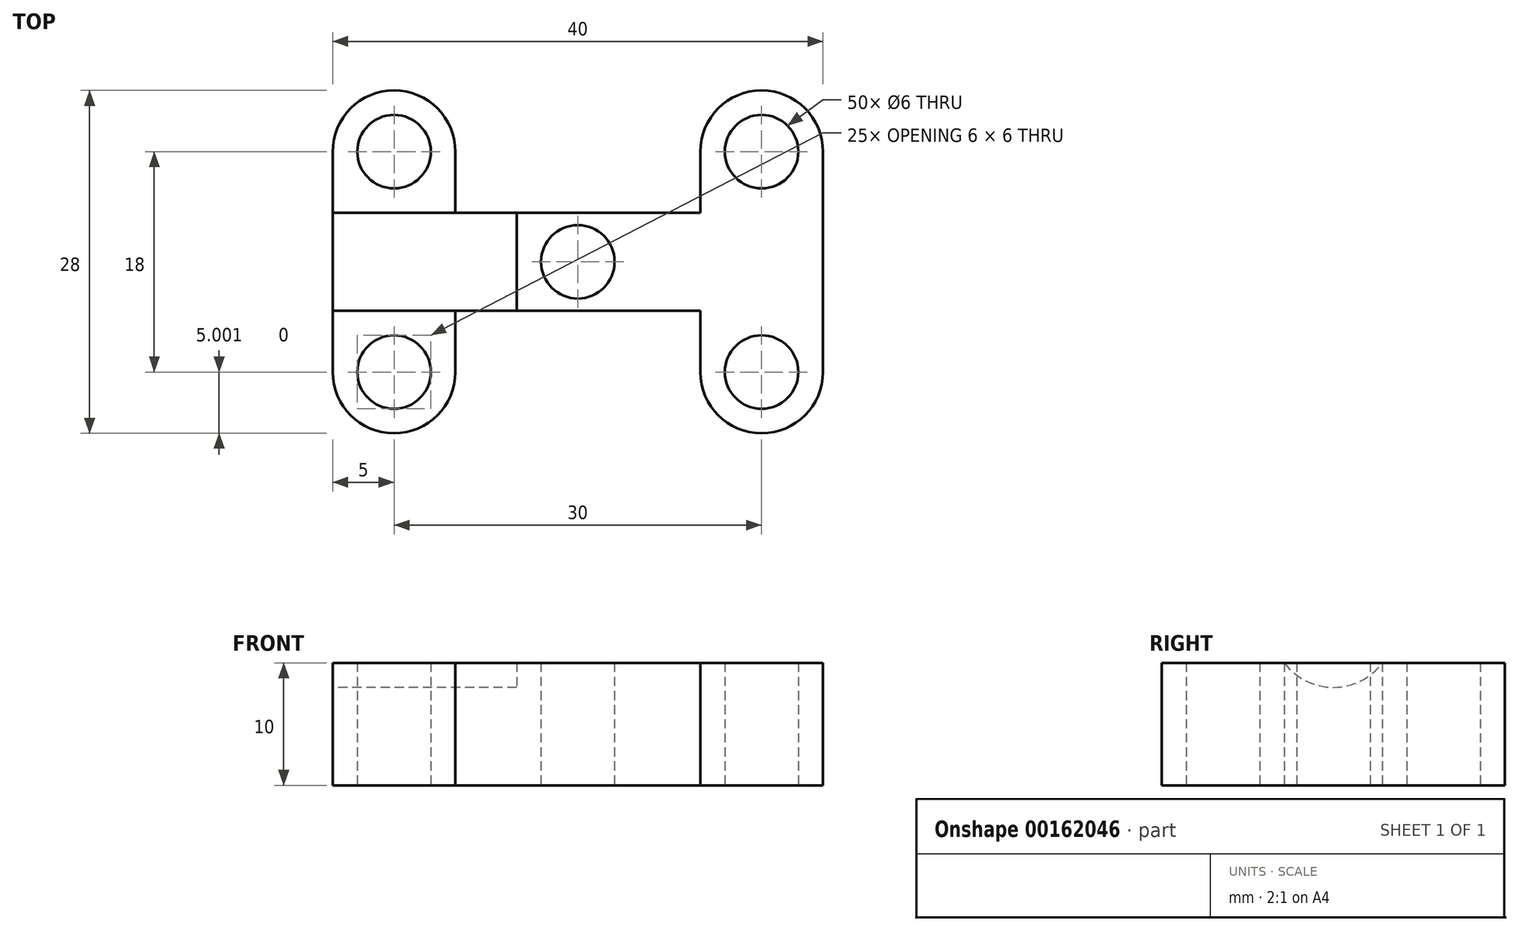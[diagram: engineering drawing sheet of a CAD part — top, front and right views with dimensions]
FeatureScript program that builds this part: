
annotation { "Feature Type Name" : "Feature", "Feature Type Description" : "" }
export const myFeature = defineFeature(function(context is Context, id is Id, definition is map)
    precondition{}
    {
        {
            var Q0;
            Q0=qCreatedBy(makeId("Front.planeOp"),FACE);
            var sketch = newSketch(context, id + "F0", { "sketchPlane" : qUnion([Q0])});
            skLineSegment(sketch, "E0.bottom", {"start": v(-25, 5) * mm, "end": v(25, 5) * mm});
            skLineSegment(sketch, "E0.top", {"start": v(-25, -5) * mm, "end": v(25, -5) * mm});
            skLineSegment(sketch, "E0.left", {"start": v(-25, 5) * mm, "end": v(-25, -5) * mm});
            skLineSegment(sketch, "E0.right", {"start": v(25, 5) * mm, "end": v(25, -5) * mm});
            skPoint(sketch, "E0.middle", {"position": v(0, 0) * mm});
            skLineSegment(sketch, "E1.bottom", {"start": v(-25, 5) * mm, "end": v(-10, 5) * mm});
            skLineSegment(sketch, "E1.top", {"start": v(-25, 90) * mm, "end": v(-10, 90) * mm});
            skLineSegment(sketch, "E1.left", {"start": v(-25, 5) * mm, "end": v(-25, 90) * mm});
            skLineSegment(sketch, "E1.right", {"start": v(-10, 5) * mm, "end": v(-10, 90) * mm});
            skLineSegment(sketch, "E2.MirrorCS", {"start": v(10, 5) * mm, "end": v(10, 90) * mm});
            skLineSegment(sketch, "E3.MirrorCS", {"start": v(25, 5) * mm, "end": v(25, 90) * mm});
            skLineSegment(sketch, "E4.MirrorCS", {"start": v(25, 5) * mm, "end": v(10, 5) * mm});
            skLineSegment(sketch, "E5.MirrorCS", {"start": v(25, 90) * mm, "end": v(10, 90) * mm});
            skPoint(sketch, "E6", {"position": v(-17.5, 80) * mm});
            skPoint(sketch, "E6.positionSnap0", {"position": v(-17.5, 90) * mm});
            skPoint(sketch, "E7.MirrorP", {"position": v(17.5, 80) * mm});
            skLineSegment(sketch, "E8", {"start": v(10, 5) * mm, "end": v(10, -5) * mm});
            skLineSegment(sketch, "E9", {"start": v(-10, 5) * mm, "end": v(-10, -5) * mm});
            skLineSegment(sketch, "E10.bottom", {"start": v(-25, 90) * mm, "end": v(25, 90) * mm});
            skLineSegment(sketch, "E10.top", {"start": v(-25, 95) * mm, "end": v(25, 95) * mm});
            skLineSegment(sketch, "E10.left", {"start": v(-25, 90) * mm, "end": v(-25, 95) * mm});
            skLineSegment(sketch, "E10.right", {"start": v(25, 90) * mm, "end": v(25, 95) * mm});
            skLineSegment(sketch, "E11", {"start": v(-10, 90) * mm, "end": v(-10, 95) * mm});
            skLineSegment(sketch, "E12", {"start": v(10, 90) * mm, "end": v(10, 95) * mm});
            skPoint(sketch, "E12.endSnap0", {"position": v(0, 95) * mm});
            skSolve(sketch);
        }
        {
            var Q0;
            Q0=qCreatedBy(makeId("Top.planeOp"),FACE);
            var sketch = newSketch(context, id + "F1", { "sketchPlane" : qUnion([Q0])});
            skLineSegment(sketch, "E13", {"start": v(-25, -6.7) * mm, "end": v(25, -6.7) * mm});
            skLineSegment(sketch, "E14", {"start": v(-25, -14.7) * mm, "end": v(15, -14.7) * mm});
            skLineSegment(sketch, "E15.bottom", {"start": v(-25, 3.3) * mm, "end": v(15, 3.3) * mm});
            skLineSegment(sketch, "E15.top", {"start": v(-25, -24.7) * mm, "end": v(15, -24.7) * mm});
            skLineSegment(sketch, "E15.left", {"start": v(-25, 3.3) * mm, "end": v(-25, -24.7) * mm});
            skLineSegment(sketch, "E15.right", {"start": v(15, 3.3) * mm, "end": v(15, -24.7) * mm});
            skLineSegment(sketch, "E16", {"start": v(-15, 3.3) * mm, "end": v(-15, -24.7) * mm});
            skLineSegment(sketch, "E17", {"start": v(5, 3.3) * mm, "end": v(5, -24.7) * mm});
            skPoint(sketch, "E18", {"position": v(10, -19.7) * mm});
            skLineSegment(sketch, "E19", {"start": v(-25, -10.7) * mm, "end": v(15, -10.7) * mm, "construction": true});
            skPoint(sketch, "E20.MirrorP", {"position": v(10, -1.7) * mm});
            skPoint(sketch, "E21", {"position": v(-5, -10.7) * mm});
            skLineSegment(sketch, "E22", {"start": v(-5, 3.3) * mm, "end": v(-5, -24.7) * mm, "construction": true});
            skPoint(sketch, "E23.MirrorP", {"position": v(-20, -1.7) * mm});
            skPoint(sketch, "E24.MirrorP", {"position": v(-20, -19.7) * mm});
            skSolve(sketch);
        }
        {
            var Q0;
            {var subQ0=sQuery(id+"F1.wireOp",EDGE,"E15.left");var subQ1=sQuery(id+"F1.wireOp",EDGE,"E13");var subQ2=makeQuery(id+"F1.imprint","INTERSECT",VERTEX,{"derivedFrom":[subQ1,subQ0]});Q0=makeQuery(id+"F1.imprint","IMPRINT",FACE,{"disambiguationData":[TD([[makeQuery(id+"F1.imprint","IMPRINT",EDGE,{"disambiguationData":[TD([[subQ2,-1.0]])],"derivedFrom":subQ1}),1.0]])]});}
            var Q1;
            {var subQ0=sQuery(id+"F1.wireOp",EDGE,"E15.left");var subQ1=sQuery(id+"F1.wireOp",EDGE,"E14");var subQ2=makeQuery(id+"F1.imprint","INTERSECT",VERTEX,{"derivedFrom":[subQ1,subQ0]});Q1=makeQuery(id+"F1.imprint","IMPRINT",FACE,{"disambiguationData":[TD([[makeQuery(id+"F1.imprint","IMPRINT",EDGE,{"disambiguationData":[TD([[subQ2,-1.0]])],"derivedFrom":subQ1}),-1.0]])]});}
            var Q2;
            {var subQ0=sQuery(id+"F1.wireOp",EDGE,"E15.right");var subQ1=sQuery(id+"F1.wireOp",EDGE,"E13");var subQ2=makeQuery(id+"F1.imprint","INTERSECT",VERTEX,{"derivedFrom":[subQ1,subQ0]});Q2=makeQuery(id+"F1.imprint","IMPRINT",FACE,{"disambiguationData":[TD([[makeQuery(id+"F1.imprint","IMPRINT",EDGE,{"disambiguationData":[TD([[subQ2,1.0]])],"derivedFrom":subQ1}),1.0]])]});}
            var Q3;
            {var subQ0=sQuery(id+"F1.wireOp",EDGE,"E15.right");var subQ1=sQuery(id+"F1.wireOp",EDGE,"E14");var subQ2=makeQuery(id+"F1.imprint","INTERSECT",VERTEX,{"derivedFrom":[subQ1,subQ0]});Q3=makeQuery(id+"F1.imprint","IMPRINT",FACE,{"disambiguationData":[TD([[makeQuery(id+"F1.imprint","IMPRINT",EDGE,{"disambiguationData":[TD([[subQ2,1.0]])],"derivedFrom":subQ1}),-1.0]])]});}
            extrude(context, id + "F2", {"entities" : qUnion([Q0, Q1, Q2, Q3]), "depth" : 10 * mm});
        }
        {
            var Q0;
            {var subQ0=sQuery(id+"F1.wireOp",EDGE,"E15.left");var subQ1=sQuery(id+"F1.wireOp",EDGE,"E13");var subQ2=makeQuery(id+"F1.imprint","INTERSECT",VERTEX,{"derivedFrom":[subQ1,subQ0]});Q0=makeQuery(id+"F1.imprint","IMPRINT",FACE,{"disambiguationData":[TD([[makeQuery(id+"F1.imprint","IMPRINT",EDGE,{"disambiguationData":[TD([[subQ2,-1.0]])],"derivedFrom":subQ1}),-1.0]])]});}
            var Q1;
            {var subQ0=sQuery(id+"F1.wireOp",EDGE,"E16");var subQ1=sQuery(id+"F1.wireOp",EDGE,"E13");var subQ2=makeQuery(id+"F1.imprint","INTERSECT",VERTEX,{"derivedFrom":[subQ1,subQ0]});Q1=makeQuery(id+"F1.imprint","IMPRINT",FACE,{"disambiguationData":[TD([[makeQuery(id+"F1.imprint","IMPRINT",EDGE,{"disambiguationData":[TD([[subQ2,-1.0]])],"derivedFrom":subQ1}),-1.0]])]});}
            var Q2;
            {var subQ0=sQuery(id+"F1.wireOp",EDGE,"E15.right");var subQ1=sQuery(id+"F1.wireOp",EDGE,"E13");var subQ2=makeQuery(id+"F1.imprint","INTERSECT",VERTEX,{"derivedFrom":[subQ1,subQ0]});Q2=makeQuery(id+"F1.imprint","IMPRINT",FACE,{"disambiguationData":[TD([[makeQuery(id+"F1.imprint","IMPRINT",EDGE,{"disambiguationData":[TD([[subQ2,1.0]])],"derivedFrom":subQ1}),-1.0]])]});}
            extrude(context, id + "F3", {"entities" : qUnion([Q0, Q1, Q2]), "depth" : 10 * mm});
        }
        {
            var Q0;
            Q0=makeQuery(id+"F3.opExtrude","SWEPT_FACE",FACE,{"disambiguationData":[OSD([sQuery(id+"F1.wireOp",EDGE,"E15.left")])]});
            var sketch = newSketch(context, id + "F4", { "sketchPlane" : qUnion([Q0])});
            skArc(sketch, "E25", {"start": v(6.7, 10) * mm, "mid": v(10.7, 8) * mm, "end": v(14.7, 10) * mm});
            skSolve(sketch);
        }
        {
            var Q0;
            Q0=makeQuery(id+"F4.imprint","IMPRINT",FACE,{"disambiguationData":[TD([[makeQuery(id+"F4.imprint","IMPRINT",EDGE,{"derivedFrom":sQuery(id+"F4.wireOp",EDGE,"E25")}),1.0]])]});
            extrude(context, id + "F5", {"entities" : qUnion([Q0]), "operationType" : NewBodyOperationType.REMOVE, "oppositeDirection" : true, "depth" : 15 * mm});
        }
        {
            var Q0;
            Q0=sQuery(id+"F1.wireOp",VERTEX,"E23.MirrorP");
            var Q1;
            Q1=sQuery(id+"F1.wireOp",VERTEX,"E21");
            var Q2;
            Q2=sQuery(id+"F1.wireOp",VERTEX,"E20.MirrorP");
            var Q3;
            Q3=sQuery(id+"F1.wireOp",VERTEX,"E18");
            var Q4;
            Q4=sQuery(id+"F1.wireOp",VERTEX,"E24.MirrorP");
            var Q5;
            Q5=makeQuery(id+"F2.opExtrude","SWEPT_BODY",BODY,{"disambiguationData":[OSD([sQuery(id+"F1.wireOp",EDGE,"E13"),sQuery(id+"F1.wireOp",EDGE,"E15.bottom"),sQuery(id+"F1.wireOp",EDGE,"E15.left"),sQuery(id+"F1.wireOp",EDGE,"E15.right")])]});
            var Q6;
            Q6=makeQuery(id+"F3.opExtrude","SWEPT_BODY",BODY,{"disambiguationData":[OSD([sQuery(id+"F1.wireOp",EDGE,"E13"),sQuery(id+"F1.wireOp",EDGE,"E14"),sQuery(id+"F1.wireOp",EDGE,"E15.left"),sQuery(id+"F1.wireOp",EDGE,"E15.right")])]});
            var Q7;
            Q7=makeQuery(id+"F2.opExtrude","SWEPT_BODY",BODY,{"disambiguationData":[OSD([sQuery(id+"F1.wireOp",EDGE,"E14"),sQuery(id+"F1.wireOp",EDGE,"E15.top"),sQuery(id+"F1.wireOp",EDGE,"E15.left"),sQuery(id+"F1.wireOp",EDGE,"E15.right")])]});
            hole(context, id + "F6", {"style" : HoleStyle.SIMPLE, "endStyle" : HoleEndStyle.BLIND, "oppositeDirection" : true, "holeDiameter" : 6 * mm, "holeDepth" : 20 * mm, "locations" : qUnion([Q0, Q1, Q2, Q3, Q4]), "scope" : qUnion([Q5, Q6, Q7])});
        }
        {
            var Q0;
            Q0=makeQuery(id+"F2.opExtrude","SWEPT_EDGE",EDGE,{"disambiguationData":[OSD([sQuery(id+"F1.wireOp",EDGE,"E15.bottom"),sQuery(id+"F1.wireOp",EDGE,"E15.left")])]});
            var Q1;
            Q1=makeQuery(id+"F2.opExtrude","SWEPT_EDGE",EDGE,{"disambiguationData":[OSD([sQuery(id+"F1.wireOp",EDGE,"E15.top"),sQuery(id+"F1.wireOp",EDGE,"E15.left")])]});
            var Q2;
            Q2=makeQuery(id+"F2.opExtrude","SWEPT_EDGE",EDGE,{"disambiguationData":[OSD([sQuery(id+"F1.wireOp",EDGE,"E15.top"),sQuery(id+"F1.wireOp",EDGE,"E15.right")])]});
            var Q3;
            Q3=makeQuery(id+"F2.opExtrude","SWEPT_EDGE",EDGE,{"disambiguationData":[OSD([sQuery(id+"F1.wireOp",EDGE,"E15.bottom"),sQuery(id+"F1.wireOp",EDGE,"E15.right")])]});
            fillet(context, id + "F7", {"entities" : qUnion([Q0, Q1, Q2, Q3]), "radius" : 5 * mm, "tangentPropagation" : true, "allowEdgeOverflow" : false});
        }
        {
            var Q0;
            Q0=makeQuery(id+"F2.opExtrude","SWEPT_BODY",BODY,{"disambiguationData":[OSD([sQuery(id+"F1.wireOp",EDGE,"E13"),sQuery(id+"F1.wireOp",EDGE,"E15.bottom"),sQuery(id+"F1.wireOp",EDGE,"E15.left"),sQuery(id+"F1.wireOp",EDGE,"E15.right")])]});
            var Q1;
            Q1=makeQuery(id+"F3.opExtrude","SWEPT_BODY",BODY,{"disambiguationData":[OSD([sQuery(id+"F1.wireOp",EDGE,"E13"),sQuery(id+"F1.wireOp",EDGE,"E14"),sQuery(id+"F1.wireOp",EDGE,"E15.left"),sQuery(id+"F1.wireOp",EDGE,"E15.right")])]});
            var Q2;
            Q2=makeQuery(id+"F2.opExtrude","SWEPT_BODY",BODY,{"disambiguationData":[OSD([sQuery(id+"F1.wireOp",EDGE,"E14"),sQuery(id+"F1.wireOp",EDGE,"E15.top"),sQuery(id+"F1.wireOp",EDGE,"E15.left"),sQuery(id+"F1.wireOp",EDGE,"E15.right")])]});
            booleanBodies(context, id + "F8", {"operationType" : BooleanOperationType.UNION, "tools" : qUnion([Q0, Q1, Q2])});
        }
        {
            var Q0;
            Q0=makeQuery(id+"F2.opExtrude","SWEPT_EDGE",EDGE,{"disambiguationData":[OSD([sQuery(id+"F1.wireOp",EDGE,"E15.bottom"),sQuery(id+"F1.wireOp",EDGE,"E16")])]});
            var Q1;
            Q1=makeQuery(id+"F2.opExtrude","SWEPT_EDGE",EDGE,{"disambiguationData":[OSD([sQuery(id+"F1.wireOp",EDGE,"E15.bottom"),sQuery(id+"F1.wireOp",EDGE,"E17")])]});
            var Q2;
            Q2=makeQuery(id+"F2.opExtrude","SWEPT_EDGE",EDGE,{"disambiguationData":[OSD([sQuery(id+"F1.wireOp",EDGE,"E15.top"),sQuery(id+"F1.wireOp",EDGE,"E16")])]});
            var Q3;
            Q3=makeQuery(id+"F2.opExtrude","SWEPT_EDGE",EDGE,{"disambiguationData":[OSD([sQuery(id+"F1.wireOp",EDGE,"E15.top"),sQuery(id+"F1.wireOp",EDGE,"E17")])]});
            var Q4;
            Q4=makeQuery(id+"F2.opExtrude","SWEPT_EDGE",EDGE,{"disambiguationData":[OSD([sQuery(id+"F1.wireOp",EDGE,"E14"),sQuery(id+"F1.wireOp",EDGE,"E16")])]});
            var Q5;
            Q5=makeQuery(id+"F2.opExtrude","SWEPT_EDGE",EDGE,{"disambiguationData":[OSD([sQuery(id+"F1.wireOp",EDGE,"E14"),sQuery(id+"F1.wireOp",EDGE,"E17")])]});
            var Q6;
            Q6=makeQuery(id+"F2.opExtrude","SWEPT_EDGE",EDGE,{"disambiguationData":[OSD([sQuery(id+"F1.wireOp",EDGE,"E13"),sQuery(id+"F1.wireOp",EDGE,"E17")])]});
            var Q7;
            Q7=makeQuery(id+"F2.opExtrude","SWEPT_EDGE",EDGE,{"disambiguationData":[OSD([sQuery(id+"F1.wireOp",EDGE,"E13"),sQuery(id+"F1.wireOp",EDGE,"E16")])]});
            fillet(context, id + "F9", {"entities" : qUnion([Q0, Q1, Q2, Q3, Q4, Q5, Q6, Q7]), "radius" : 5 * mm, "tangentPropagation" : true, "allowEdgeOverflow" : false});
        }
    });
